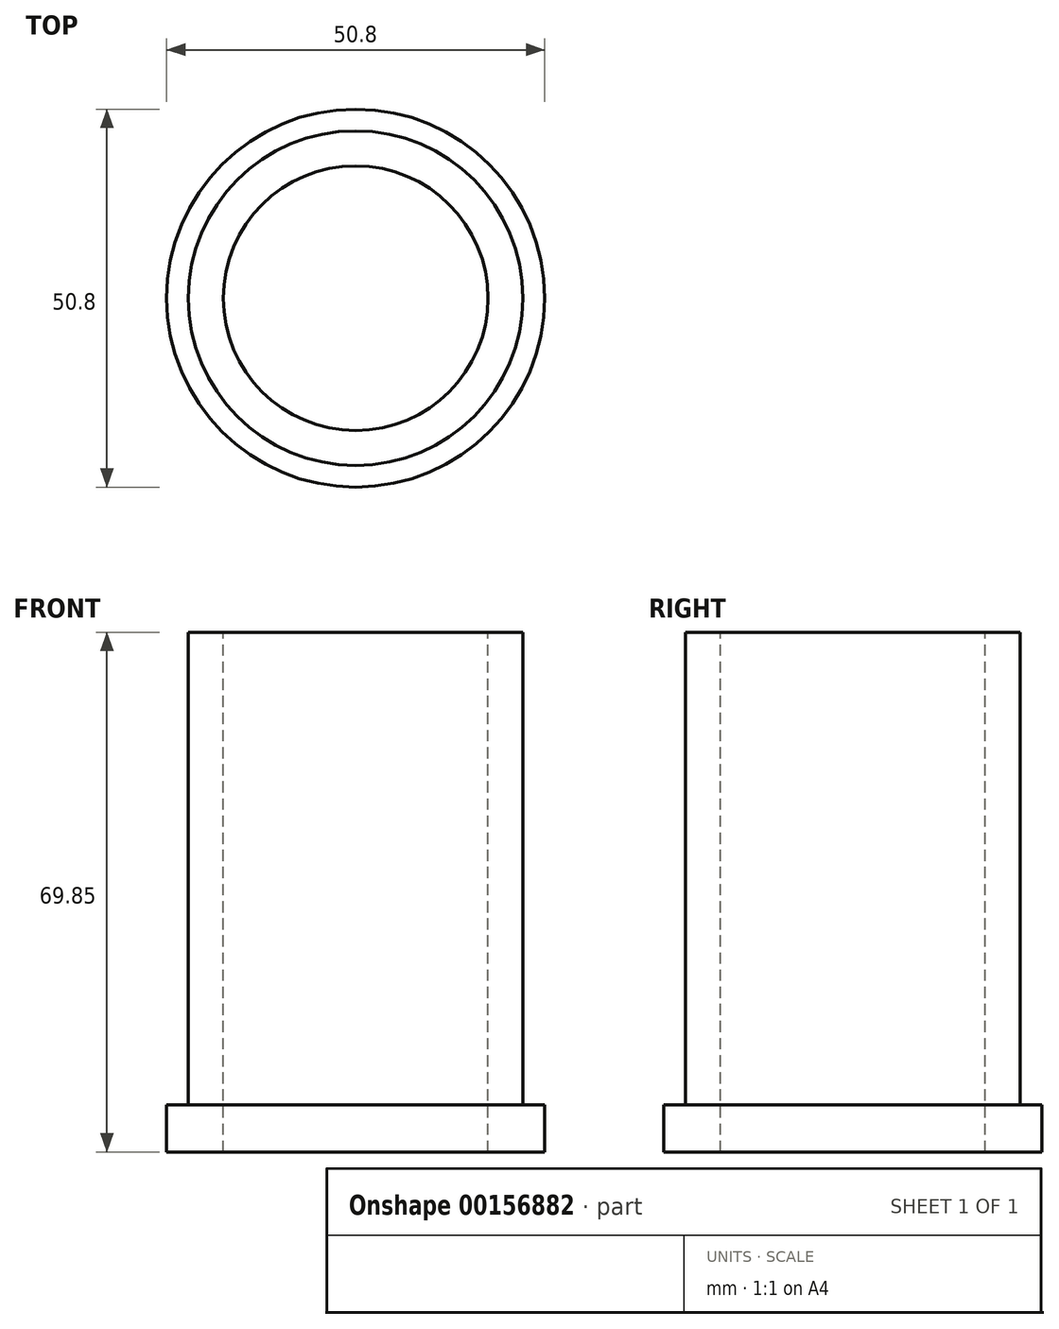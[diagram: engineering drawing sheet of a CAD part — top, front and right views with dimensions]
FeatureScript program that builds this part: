
annotation { "Feature Type Name" : "Feature", "Feature Type Description" : "" }
export const myFeature = defineFeature(function(context is Context, id is Id, definition is map)
    precondition{}
    {
        {
            var Q0;
            Q0=qCreatedBy(makeId("Front.planeOp"),FACE);
            var sketch = newSketch(context, id + "F0", { "sketchPlane" : qUnion([Q0])});
            skLineSegment(sketch, "E0", {"start": v(17.78, 0) * mm, "end": v(25.4, 0) * mm});
            skLineSegment(sketch, "E1", {"start": v(25.4, 0) * mm, "end": v(25.4, 6.35) * mm});
            skLineSegment(sketch, "E2", {"start": v(25.4, 6.35) * mm, "end": v(22.48, 6.35) * mm});
            skLineSegment(sketch, "E3", {"start": v(22.48, 6.35) * mm, "end": v(22.48, 69.85) * mm});
            skLineSegment(sketch, "E4", {"start": v(22.48, 69.85) * mm, "end": v(17.78, 69.85) * mm});
            skLineSegment(sketch, "E5", {"start": v(17.78, 69.85) * mm, "end": v(17.78, 0) * mm});
            skLineSegment(sketch, "E6", {"start": v(0, 74.05) * mm, "end": v(0, -27.56) * mm, "construction": true});
            skSolve(sketch);
        }
        {
            var Q0;
            Q0=makeQuery(id+"F0.imprint","IMPRINT",FACE,{"disambiguationData":[TD([[makeQuery(id+"F0.imprint","IMPRINT",EDGE,{"derivedFrom":sQuery(id+"F0.wireOp",EDGE,"E0")}),1.0]])]});
            var Q1;
            Q1=sQuery(id+"F0.wireOp",EDGE,"E6");
            revolve(context, id + "F1", {"entities" : qUnion([Q0]), "axis" : qUnion([Q1]), "revolveType" : RevolveType.FULL});
        }
    });
